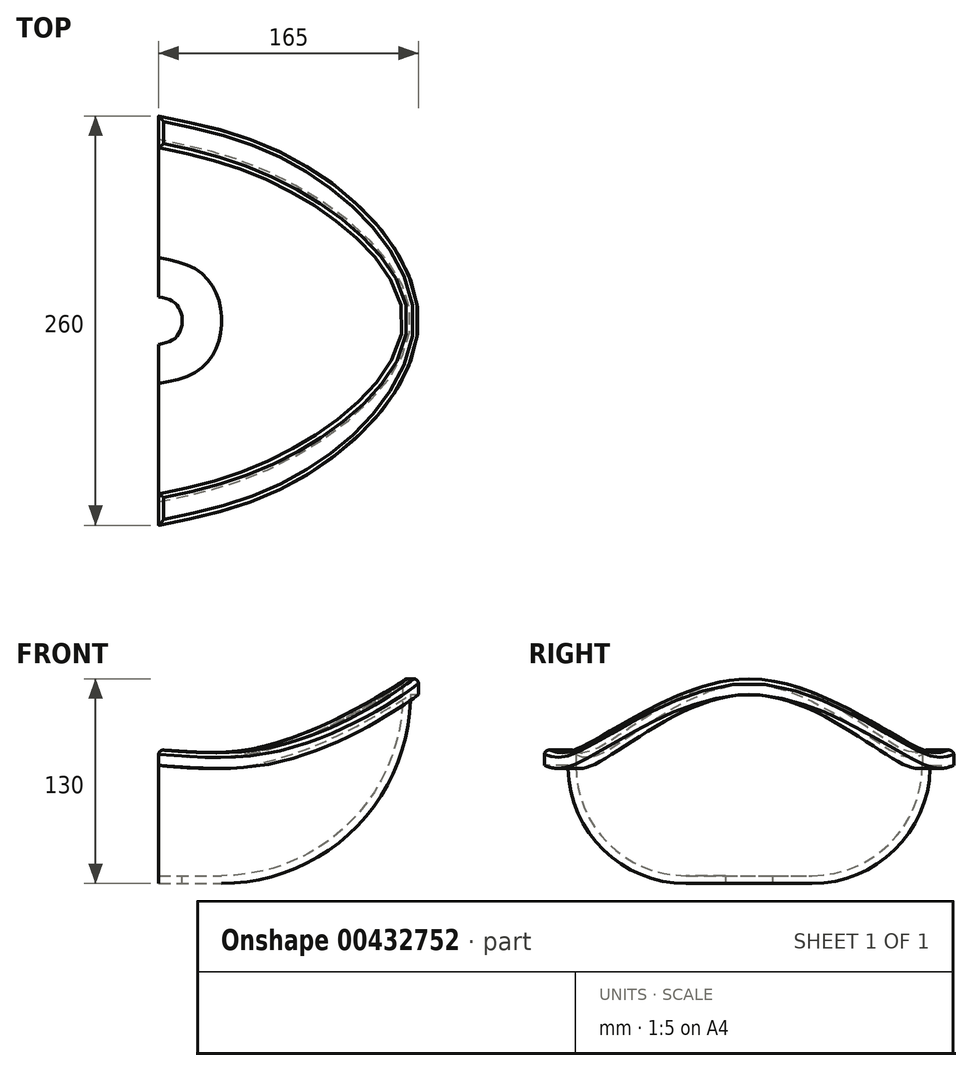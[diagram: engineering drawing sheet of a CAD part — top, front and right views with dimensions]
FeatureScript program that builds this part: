
annotation { "Feature Type Name" : "Feature", "Feature Type Description" : "" }
export const myFeature = defineFeature(function(context is Context, id is Id, definition is map)
    precondition{}
    {
        {
            var Q0;
            Q0=qCreatedBy(makeId("Front.planeOp"),FACE);
            var sketch = newSketch(context, id + "F0", { "sketchPlane" : qUnion([Q0])});
            skLineSegment(sketch, "E0.bottom", {"start": v(15, 5) * mm, "end": v(40, 5) * mm});
            skLineSegment(sketch, "E0.top", {"start": v(15, 0) * mm, "end": v(40, 0) * mm});
            skLineSegment(sketch, "E0.left", {"start": v(15, 5) * mm, "end": v(15, 0) * mm});
            skLineSegment(sketch, "E0.right", {"start": v(40, 5) * mm, "end": v(40, 0) * mm, "construction": true});
            skLineSegment(sketch, "E1.bottom", {"start": v(155, 130) * mm, "end": v(165, 130) * mm});
            skLineSegment(sketch, "E1.top", {"start": v(160, 120) * mm, "end": v(165, 120) * mm});
            skLineSegment(sketch, "E1.left", {"start": v(155, 130) * mm, "end": v(155, 120) * mm});
            skLineSegment(sketch, "E1.right", {"start": v(165, 130) * mm, "end": v(165, 120) * mm});
            skArc(sketch, "E2", {"start": v(40, 0) * mm, "mid": v(124.85, 35.15) * mm, "end": v(160, 120) * mm});
            skArc(sketch, "E3", {"start": v(40, 5) * mm, "mid": v(121.32, 38.68) * mm, "end": v(155, 120) * mm});
            skLineSegment(sketch, "E4", {"start": v(0, 0) * mm, "end": v(0, 50) * mm, "construction": true});
            skSolve(sketch);
        }
        {
            var Q0;
            Q0=sQuery(id+"F0.wireOp",EDGE,"E4");
            cPlane(context, id + "F1", {"entities" : qUnion([Q0]), "cplaneType" : CPlaneType.LINE_ANGLE, "offset" : 25 * mm, "angle" : 30 * degree, "oppositeDirection" : true, "width" : 150 * mm, "height" : 150 * mm});
        }
        {
            var Q0;
            Q0=qCreatedBy(id+"F1.planeOp",FACE);
            var sketch = newSketch(context, id + "F2", { "sketchPlane" : qUnion([Q0])});
            skLineSegment(sketch, "E5.bottom", {"start": v(15, 5) * mm, "end": v(40, 5) * mm});
            skLineSegment(sketch, "E5.top", {"start": v(15, 0) * mm, "end": v(40, 0) * mm});
            skLineSegment(sketch, "E5.left", {"start": v(15, 5) * mm, "end": v(15, 0) * mm});
            skLineSegment(sketch, "E5.right", {"start": v(40, 5) * mm, "end": v(40, 0) * mm, "construction": true});
            skLineSegment(sketch, "E6.bottom", {"start": v(110, 85) * mm, "end": v(130, 85) * mm});
            skLineSegment(sketch, "E6.top", {"start": v(115, 75) * mm, "end": v(130, 75) * mm});
            skLineSegment(sketch, "E6.left", {"start": v(110, 85) * mm, "end": v(110, 75) * mm});
            skLineSegment(sketch, "E6.right", {"start": v(130, 85) * mm, "end": v(130, 75) * mm});
            skArc(sketch, "E7", {"start": v(40, 0) * mm, "mid": v(93.03, 21.97) * mm, "end": v(115, 75) * mm});
            skArc(sketch, "E8", {"start": v(40, 5) * mm, "mid": v(89.5, 25.5) * mm, "end": v(110, 75) * mm});
            skLineSegment(sketch, "E9", {"start": v(0, 0) * mm, "end": v(0, 50) * mm, "construction": true});
            skSolve(sketch);
        }
        {
            var Q0;
            Q0=sQuery(id+"F2.wireOp",EDGE,"E9");
            cPlane(context, id + "F3", {"entities" : qUnion([Q0]), "cplaneType" : CPlaneType.LINE_ANGLE, "offset" : 150 * mm, "angle" : 150 * degree, "oppositeDirection" : true, "width" : 150 * mm, "height" : 150 * mm});
        }
        {
            var Q0;
            Q0=qCreatedBy(id+"F3.planeOp",FACE);
            var sketch = newSketch(context, id + "F4", { "sketchPlane" : qUnion([Q0])});
            skLineSegment(sketch, "E10.bottom", {"start": v(15, 5) * mm, "end": v(40, 5) * mm});
            skLineSegment(sketch, "E10.top", {"start": v(15, 0) * mm, "end": v(40, 0) * mm});
            skLineSegment(sketch, "E10.left", {"start": v(15, 5) * mm, "end": v(15, 0) * mm});
            skLineSegment(sketch, "E10.right", {"start": v(40, 5) * mm, "end": v(40, 0) * mm, "construction": true});
            skLineSegment(sketch, "E11.bottom", {"start": v(110, 85) * mm, "end": v(130, 85) * mm});
            skLineSegment(sketch, "E11.top", {"start": v(115, 75) * mm, "end": v(130, 75) * mm});
            skLineSegment(sketch, "E11.left", {"start": v(110, 85) * mm, "end": v(110, 75) * mm});
            skLineSegment(sketch, "E11.right", {"start": v(130, 85) * mm, "end": v(130, 75) * mm});
            skArc(sketch, "E12", {"start": v(40, 0) * mm, "mid": v(93.03, 21.97) * mm, "end": v(115, 75) * mm});
            skArc(sketch, "E13", {"start": v(40, 5) * mm, "mid": v(89.5, 25.5) * mm, "end": v(110, 75) * mm});
            skLineSegment(sketch, "E14", {"start": v(0, 0) * mm, "end": v(0, 50) * mm, "construction": true});
            skSolve(sketch);
        }
        {
            var Q0;
            Q0=qCreatedBy(makeId("Right.planeOp"),FACE);
            var sketch = newSketch(context, id + "F5", { "sketchPlane" : qUnion([Q0])});
            skLineSegment(sketch, "E15.bottom", {"start": v(15, 5) * mm, "end": v(40, 5) * mm});
            skLineSegment(sketch, "E15.top", {"start": v(15, 0) * mm, "end": v(40, 0) * mm});
            skLineSegment(sketch, "E15.left", {"start": v(15, 5) * mm, "end": v(15, 0) * mm});
            skLineSegment(sketch, "E15.right", {"start": v(40, 5) * mm, "end": v(40, 0) * mm, "construction": true});
            skLineSegment(sketch, "E16.bottom", {"start": v(110, 85) * mm, "end": v(130, 85) * mm});
            skLineSegment(sketch, "E16.top", {"start": v(115, 75) * mm, "end": v(130, 75) * mm});
            skLineSegment(sketch, "E16.left", {"start": v(110, 85) * mm, "end": v(110, 75) * mm});
            skLineSegment(sketch, "E16.right", {"start": v(130, 85) * mm, "end": v(130, 75) * mm});
            skArc(sketch, "E17", {"start": v(40, 0) * mm, "mid": v(93.03, 21.97) * mm, "end": v(115, 75) * mm});
            skArc(sketch, "E18", {"start": v(40, 5) * mm, "mid": v(89.5, 25.5) * mm, "end": v(110, 75) * mm});
            skLineSegment(sketch, "E19", {"start": v(0, 0) * mm, "end": v(0, 50) * mm, "construction": true});
            skSolve(sketch);
        }
        {
            var Q0;
            Q0=sQuery(id+"F5.wireOp",EDGE,"E19");
            cPlane(context, id + "F6", {"entities" : qUnion([Q0]), "cplaneType" : CPlaneType.LINE_ANGLE, "offset" : 25 * mm, "angle" : 180 * degree, "width" : 150 * mm, "height" : 150 * mm});
        }
        {
            var Q0;
            Q0=qCreatedBy(id+"F6.planeOp",FACE);
            var sketch = newSketch(context, id + "F7", { "sketchPlane" : qUnion([Q0])});
            skLineSegment(sketch, "E20.bottom", {"start": v(15, 5) * mm, "end": v(40, 5) * mm});
            skLineSegment(sketch, "E20.top", {"start": v(15, 0) * mm, "end": v(40, 0) * mm});
            skLineSegment(sketch, "E20.left", {"start": v(15, 5) * mm, "end": v(15, 0) * mm});
            skLineSegment(sketch, "E20.right", {"start": v(40, 5) * mm, "end": v(40, 0) * mm, "construction": true});
            skLineSegment(sketch, "E21.bottom", {"start": v(110, 85) * mm, "end": v(130, 85) * mm});
            skLineSegment(sketch, "E21.top", {"start": v(115, 75) * mm, "end": v(130, 75) * mm});
            skLineSegment(sketch, "E21.left", {"start": v(110, 85) * mm, "end": v(110, 75) * mm});
            skLineSegment(sketch, "E21.right", {"start": v(130, 85) * mm, "end": v(130, 75) * mm});
            skArc(sketch, "E22", {"start": v(40, 0) * mm, "mid": v(93.03, 21.97) * mm, "end": v(115, 75) * mm});
            skArc(sketch, "E23", {"start": v(40, 5) * mm, "mid": v(89.5, 25.5) * mm, "end": v(110, 75) * mm});
            skLineSegment(sketch, "E24", {"start": v(0, 0) * mm, "end": v(0, 50) * mm, "construction": true});
            skSolve(sketch);
        }
        {
            var Q0;
            Q0=makeQuery(id+"F7.imprint","IMPRINT",FACE,{"disambiguationData":[TD([[makeQuery(id+"F7.imprint","IMPRINT",EDGE,{"derivedFrom":sQuery(id+"F7.wireOp",EDGE,"E20.bottom")}),-1.0]])]});
            var Q1;
            Q1=makeQuery(id+"F4.imprint","IMPRINT",FACE,{"disambiguationData":[TD([[makeQuery(id+"F4.imprint","IMPRINT",EDGE,{"derivedFrom":sQuery(id+"F4.wireOp",EDGE,"E10.bottom")}),-1.0]])]});
            var Q2;
            Q2=makeQuery(id+"F0.imprint","IMPRINT",FACE,{"disambiguationData":[TD([[makeQuery(id+"F0.imprint","IMPRINT",EDGE,{"derivedFrom":sQuery(id+"F0.wireOp",EDGE,"E0.bottom")}),-1.0]])]});
            var Q3;
            Q3=makeQuery(id+"F2.imprint","IMPRINT",FACE,{"disambiguationData":[TD([[makeQuery(id+"F2.imprint","IMPRINT",EDGE,{"derivedFrom":sQuery(id+"F2.wireOp",EDGE,"E5.bottom")}),-1.0]])]});
            var Q4;
            Q4=makeQuery(id+"F5.imprint","IMPRINT",FACE,{"disambiguationData":[TD([[makeQuery(id+"F5.imprint","IMPRINT",EDGE,{"derivedFrom":sQuery(id+"F5.wireOp",EDGE,"E15.bottom")}),-1.0]])]});
            loft(context, id + "F8", {"sheetProfilesArray" : [{ "sheetProfileEntities" : qUnion([Q0]) }, { "sheetProfileEntities" : qUnion([Q1]) }, { "sheetProfileEntities" : qUnion([Q2]) }, { "sheetProfileEntities" : qUnion([Q3]) }, { "sheetProfileEntities" : qUnion([Q4]) }]});
        }
        {
            var Q0;
            Q0=makeQuery(id+"F8.opLoft","SWEPT_FACE",FACE,{"disambiguationData":[OSD([sQuery(id+"F4.wireOp",EDGE,"E11.bottom"),sQuery(id+"F4.wireOp",EDGE,"E11.left"),sQuery(id+"F4.wireOp",EDGE,"E11.right"),sQuery(id+"F7.wireOp",EDGE,"E21.bottom"),sQuery(id+"F7.wireOp",EDGE,"E21.left"),sQuery(id+"F7.wireOp",EDGE,"E21.right")])]});
            fillet(context, id + "F9", {"entities" : qUnion([Q0]), "radius" : 3 * mm, "tangentPropagation" : true, "allowEdgeOverflow" : false});
        }
        {
            var Q0;
            Q0=qCreatedBy(id+"F3.planeOp",FACE);
            cPlane(context, id + "F10", {"entities" : qUnion([Q0]), "cplaneType" : CPlaneType.OFFSET, "offset" : 80 * mm, "oppositeDirection" : true, "width" : 150 * mm, "height" : 150 * mm});
        }
    });
